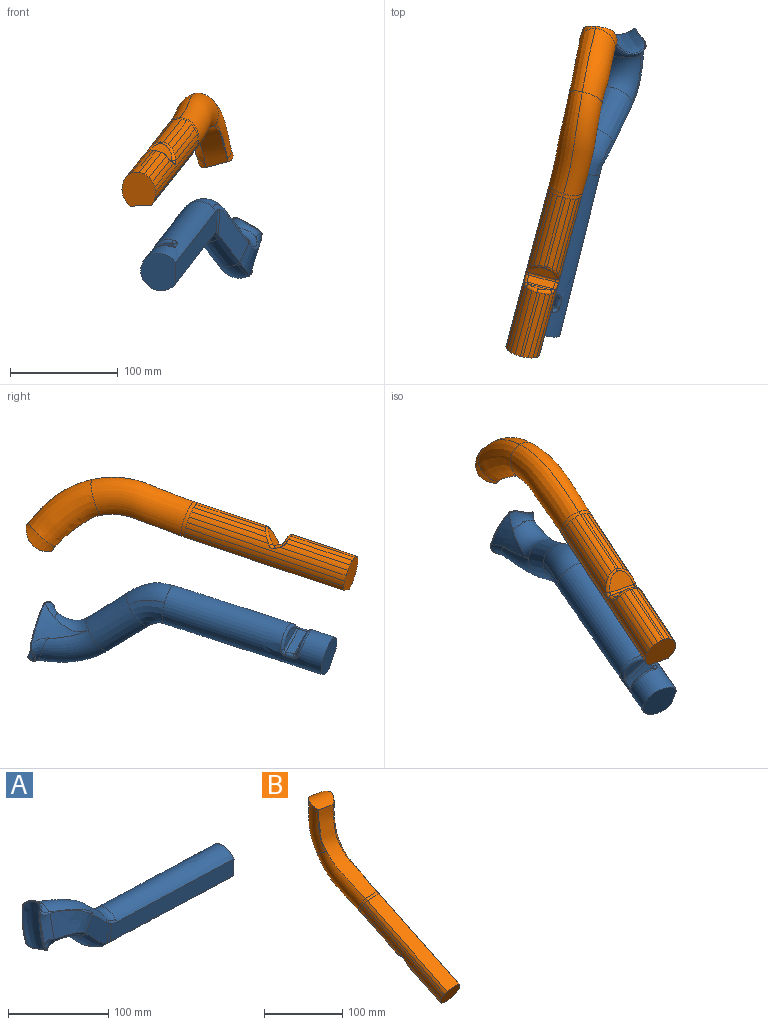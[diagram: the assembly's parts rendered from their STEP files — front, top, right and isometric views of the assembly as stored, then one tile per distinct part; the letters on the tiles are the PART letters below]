
ASSEMBLY  parts=2 mates=1
PART A: 46 faces, bbox 296.6x57.7x106.7 mm
  f0: bspline ~61.39x39.84mm, area 1710.6mm2, adj f1,f2,f3,f4,f5,f6,f7
  f1: bspline ~39.62x9.08mm, area 81.6mm2, adj f0,f5,f7,f12,f15
  f2: bspline ~36.46x7.48mm, area 63.5mm2, adj f0,f3,f6,f8
  f3: bspline ~4.7x3.74mm, area 7.1mm2, adj f0,f2,f4,f8,f10
  f4: bspline ~10.43x8.28mm, area 22.7mm2, adj f0,f3,f5,f11
  f5: bspline ~21.61x15.24mm, area 51.4mm2, adj f0,f1,f4,f12
  f6: bspline ~8.84x6.47mm, area 15.1mm2, adj f0,f2,f7,f8,f13
  f7: bspline ~29.59x11.48mm, area 71.7mm2, adj f0,f1,f6,f14,f15
  f8: bspline ~39.68x13.5mm, area 360.7mm2, adj f2,f3,f6,f10,f13,f17
  f9: bspline ~56.1x27.81mm, area 91.1mm2, adj f10,f17,f18,f19
  f10: bspline ~13.26x5.92mm, area 34.8mm2, adj f3,f8,f9,f11,f17,f19
  f11: bspline ~12.94x11.27mm, area 78.8mm2, adj f4,f10,f12,f19
  f12: bspline ~25.15x22.49mm, area 215.3mm2, adj f1,f5,f11,f15,f19
  f13: bspline ~19.23x18.07mm, area 112.5mm2, adj f6,f8,f14,f16,f17,f21
  f14: bspline ~30.36x17.31mm, area 310.5mm2, adj f7,f13,f15,f21
  f15: bspline ~61.06x57.07mm, area 682.7mm2, adj f1,f7,f12,f14,f19,f20,f21
  f16: bspline ~42.99x15.94mm, area 156.6mm2, adj f13,f17,f21,f22
  f17: bspline ~57.78x47.83mm, area 1401.1mm2, adj f8,f9,f10,f13,f16,f18,f22,f24
  f18: bspline ~4.18x3.32mm, area 10.8mm2, adj f9,f17,f19,f25
  f19: bspline ~60.04x39.96mm, area 2434mm2, adj f9,f10,f11,f12,f15,f18,f20,f25
  f20: cylinder r=36.97mm len=3.46mm, axis (0.71,0.19,0.68), area 2.5mm2, adj f15,f19,f21,f25
  f21: bspline ~41.18x34.11mm, area 1353.2mm2, adj f13,f14,f15,f16,f20,f22,f25
  f22: cylinder r=18.03mm len=3.97mm, axis (-0.7,-0.25,0.66), area 7.7mm2, adj f16,f17,f21,f25
  f23: cylinder r=15.8mm len=26.8mm, axis (0,-0.06,1), area 135.6mm2, adj f24,f28,f31,f32
  f24: plane 60.25x49.33mm, normal (0.32,-0.95,-0.06), area 1271.7mm2, adj f17,f23,f25,f28,f31
  f25: bspline ~59.52x59.5mm, area 4360.4mm2, adj f18,f19,f20,f21,f22,f24,f28,f29
  f26: plane 23.09x16.55mm, normal (0.99,0.13,-0.08), area 162mm2, adj f27,f35
  f27: cylinder r=2.2mm len=26.48mm, axis (0,-0.53,-0.85), area 87.8mm2, adj f26,f34,f36,f38
  f28: bspline ~16.16x10.78mm, area 52.4mm2, adj f23,f24,f25,f29,f32,f41
  f29: bspline ~34.57x33.78mm, area 1020.3mm2, adj f25,f28,f30,f41
  f30: bspline ~41.53x37.25mm, area 1772.7mm2, adj f25,f29,f31,f41
  f31: bspline ~32.2x18.13mm, area 179.6mm2, adj f23,f24,f25,f30,f32,f41
  f32: plane 167.52x23.38mm, normal (-0.04,-1,-0.06), area 3523.9mm2, adj f23,f28,f31,f33,f41
  f33: plane 36.55x33.82mm, normal (1,-0.02,0.01), area 1000.9mm2, adj f32,f41
  f34: bspline ~6.06x5.1mm, area 23mm2, adj f27,f35,f39,f41
  f35: bspline ~27.75x20.11mm, area 160.2mm2, adj f26,f34,f36,f41
  f36: bspline ~5.95x5.04mm, area 22.6mm2, adj f27,f35,f37,f41
  f37: cylinder r=3mm len=8.15mm, axis (1,-0.03,0), area 33.9mm2, adj f36,f38,f41,f43
  f38: plane 25.5x16.15mm, normal (0.02,0.85,-0.53), area 244.2mm2, adj f27,f37,f39,f45
  f39: cylinder r=3mm len=8.24mm, axis (1,-0.03,0), area 33.8mm2, adj f34,f38,f41,f44
  f40: bspline ~27.59x20.07mm, area 160mm2, adj f41,f42,f43,f44
  f41: bspline ~168.7x40.18mm, area 13856mm2, adj f28,f29,f30,f31,f32,f33,f34,f35
  f42: plane 22.97x16.35mm, normal (-0.98,0.17,-0.1), area 158.9mm2, adj f40,f45
  f43: bspline ~6.09x5.25mm, area 23.1mm2, adj f37,f40,f41,f45
  f44: bspline ~5.91x5.26mm, area 22.6mm2, adj f39,f40,f41,f45
  f45: cylinder r=2.2mm len=26.41mm, axis (0,0.53,0.85), area 89.5mm2, adj f38,f42,f43,f44
PART B: 54 faces, bbox 42.6x266.7x203.1 mm
  f0: plane 19.97x5.31mm, normal (0.01,0.92,0.39), area 77.6mm2, adj f1,f2,f3
  f1: bspline ~11.74x9.14mm, area 59.8mm2, adj f0,f2,f4,f8,f9,f10
  f2: bspline ~13.3x8.9mm, area 66.3mm2, adj f0,f1,f5,f6,f7,f11,f12
  f3: cylinder r=2.2mm len=24.14mm, axis (1,-0.02,0.01), area 47.2mm2, adj f0,f4,f12,f13
  f4: bspline ~5.52x4.77mm, area 17.8mm2, adj f1,f3,f8,f18,f19
  f5: cylinder r=13.75mm len=57.89mm, axis (0,0.9,0.43), area 172.5mm2, adj f2,f6,f10,f20
  f6: cylinder r=14.5mm len=58.66mm, axis (0,0.9,0.43), area 344.6mm2, adj f2,f5,f7,f20
  f7: cylinder r=16.43mm len=59.51mm, axis (0,0.9,0.43), area 345.5mm2, adj f2,f6,f11,f20
  f8: cylinder r=17.61mm len=60.03mm, axis (0,0.9,0.43), area 344mm2, adj f1,f4,f9,f19,f20
  f9: cylinder r=15.35mm len=59.21mm, axis (0,0.9,0.43), area 343mm2, adj f1,f8,f10,f20
  f10: cylinder r=13.96mm len=58.41mm, axis (0,0.9,0.43), area 343.1mm2, adj f1,f5,f9,f20
  f11: cylinder r=18.76mm len=60.73mm, axis (0,0.9,0.43), area 347.5mm2, adj f2,f7,f12,f20,f21
  f12: bspline ~5.43x5.08mm, area 18.2mm2, adj f2,f3,f11,f21,f22
  f13: plane 25.76x6.11mm, normal (0.02,0.85,-0.53), area 171mm2, adj f3,f14,f18,f22
  f14: cylinder r=2.2mm len=25.8mm, axis (-1,0.02,-0.01), area 78.8mm2, adj f13,f15,f17,f23
  f15: plane 25.56x16.07mm, normal (0,-0.37,-0.93), area 324.1mm2, adj f14,f16,f24
  f16: bspline ~18.39x14.76mm, area 83.2mm2, adj f15,f17,f24,f25,f26,f27,f28,f29
  f17: bspline ~6.42x4.22mm, area 21.5mm2, adj f14,f16,f18,f29
  f18: bspline ~7.44x5.77mm, area 29.5mm2, adj f4,f13,f17,f19,f29
  f19: cylinder r=19.78mm len=64.42mm, axis (0,0.9,0.43), area 356.7mm2, adj f4,f8,f18,f20,f29
  f20: plane 32.05x30.2mm, normal (0,-0.9,-0.43), area 872.3mm2, adj f5,f6,f7,f8,f9,f10,f11,f19
  f21: cylinder r=20.57mm len=66.27mm, axis (0,0.9,0.43), area 364.3mm2, adj f11,f12,f20,f22,f37
  f22: bspline ~7.36x5.72mm, area 29.4mm2, adj f12,f13,f21,f23,f37
  f23: bspline ~6.42x4.09mm, area 21.2mm2, adj f14,f22,f24,f37
  f24: bspline ~17.88x16.86mm, area 84.5mm2, adj f15,f16,f23,f37,f38,f39,f40,f41
  f25: cylinder r=13.96mm len=64.07mm, axis (0,0.9,0.43), area 374.2mm2, adj f16,f26,f42,f43
  f26: cylinder r=15.35mm len=66.89mm, axis (0,0.9,0.43), area 382.6mm2, adj f16,f25,f27,f43
  f27: cylinder r=17.61mm len=70.37mm, axis (0,0.9,0.43), area 397.9mm2, adj f16,f26,f28,f43
  f28: cylinder r=19.78mm len=74.22mm, axis (0,0.9,0.43), area 419.1mm2, adj f16,f27,f29,f43
  f29: cylinder r=21.09mm len=146.61mm, axis (0,0.9,0.43), area 838.7mm2, adj f16,f17,f18,f19,f20,f28,f30,f43
  f30: cylinder r=21.17mm len=146.58mm, axis (0,0.9,0.43), area 863.8mm2, adj f20,f29,f31,f43
  f31: cylinder r=19.97mm len=146.39mm, axis (0,0.9,0.43), area 860.7mm2, adj f20,f30,f32,f43
  f32: cylinder r=17.92mm len=146.03mm, axis (0,0.9,0.43), area 856.8mm2, adj f20,f31,f33,f43
  f33: plane 144.9x70.38mm, normal (-0.07,-0.43,0.9), area 3265.4mm2, adj f20,f32,f34,f44
  f34: cylinder r=18mm len=146.22mm, axis (0,0.9,0.43), area 858.8mm2, adj f20,f33,f35,f45
  f35: cylinder r=19.51mm len=145.38mm, axis (0,0.9,0.43), area 431.7mm2, adj f20,f34,f36,f45
  f36: cylinder r=20.75mm len=146.58mm, axis (0,0.9,0.43), area 861.4mm2, adj f20,f35,f37,f45
  f37: cylinder r=21.29mm len=146.61mm, axis (0,0.9,0.43), area 849.7mm2, adj f20,f21,f22,f23,f24,f36,f38,f45
  f38: cylinder r=20.57mm len=74.81mm, axis (0,0.9,0.43), area 422.1mm2, adj f24,f37,f39,f45
  f39: cylinder r=18.76mm len=70.95mm, axis (0,0.9,0.43), area 402mm2, adj f24,f38,f40,f45
  f40: cylinder r=16.43mm len=67.41mm, axis (0,0.9,0.43), area 386.3mm2, adj f24,f39,f41,f45
  f41: cylinder r=14.5mm len=64.47mm, axis (0,0.9,0.43), area 376.3mm2, adj f24,f40,f42,f45
  f42: cylinder r=13.75mm len=62.71mm, axis (0,0.9,0.43), area 186.8mm2, adj f24,f25,f41,f45
  f43: bspline ~31.81x17.75mm, area 162.3mm2, adj f25,f26,f27,f28,f29,f30,f31,f32
  f44: cylinder r=381.63mm len=21.45mm, axis (-0.99,0.16,0), area 80mm2, adj f33,f43,f45,f48
  f45: bspline ~30.64x17.36mm, area 161.8mm2, adj f34,f35,f36,f37,f38,f39,f40,f41
  f46: bspline ~99.67x71.97mm, area 3884.3mm2, adj f43,f47,f48,f49
  f47: bspline ~69.98x45.32mm, area 2773.1mm2, adj f46,f48,f50,f51
  f48: bspline ~98.26x87.73mm, area 2931.3mm2, adj f44,f46,f47,f49,f51,f52,f53
  f49: bspline ~97.96x68.73mm, area 4047.5mm2, adj f45,f46,f48,f50,f53
  f50: bspline ~80.58x40.78mm, area 2861.2mm2, adj f47,f49,f53
  f51: bspline ~34.06x12.75mm, area 366.7mm2, adj f47,f48,f52,f53
  f52: cylinder r=25mm len=41.04mm, axis (0.95,-0.3,0.09), area 905.5mm2, adj f48,f51,f53
  f53: bspline ~84.66x42.7mm, area 352mm2, adj f48,f49,f50,f51,f52
PLACE A rot(axis=(-0.6,0.78,0.16),172.7deg) t=(2008.89,7041.21,2796.21)mm
PLACE B rot(axis=(0.12,0.92,0.37),175.6deg) t=(7453.93,-2204.87,453)mm
MATE planar B.f20 <-> A.f33  axis (-0.25,-0.92,-0.31) through (-50.9,-236.41,30.32)mm
